# Revit family: Überspannungsableiter V20, 3-polig
name_source: partatom
category: Generic Models
revit_build: Autodesk Revit 2015 (Build: 20140606_1530(x64)
units: mm (PartAtom-declared; Revit-internal decimal feet)

## types (5) — shared parameters
Height = 79 mm
Length = 53 mm
Manufacturer = OBO Bettermann
Material = PA 66/6 FR HF RAL 9010
Material 2 = PA 66/6 FR HF RAL 2003
URL = http://www.obo-bettermann.com
Width = 90 mm  [stored 0.295276 ft]

## per-type parameters (varying)
| type | GTIN | Manufacturer Art.No. |
| V20-3-150 | 4012196159789 | 5095153 |
| V20-3-280 | 4012196159826 | 5095163 |
| V20-3-320 | 4012196159864 | 5095173 |
| V20-3-385 | 4012196159901 | 5095193 |
| V20-3-550 | 4012196160006 | 5095213 |

note: column(s) folded — value = type name in every type: Article Type

note: [stored X ft] marks values corroborated as IEEE doubles in the binary element streams (Revit-internal decimal feet)

## geometry (parser evidence)
native form markers: Sweep x2
no freeform markers — native parametric forms only
